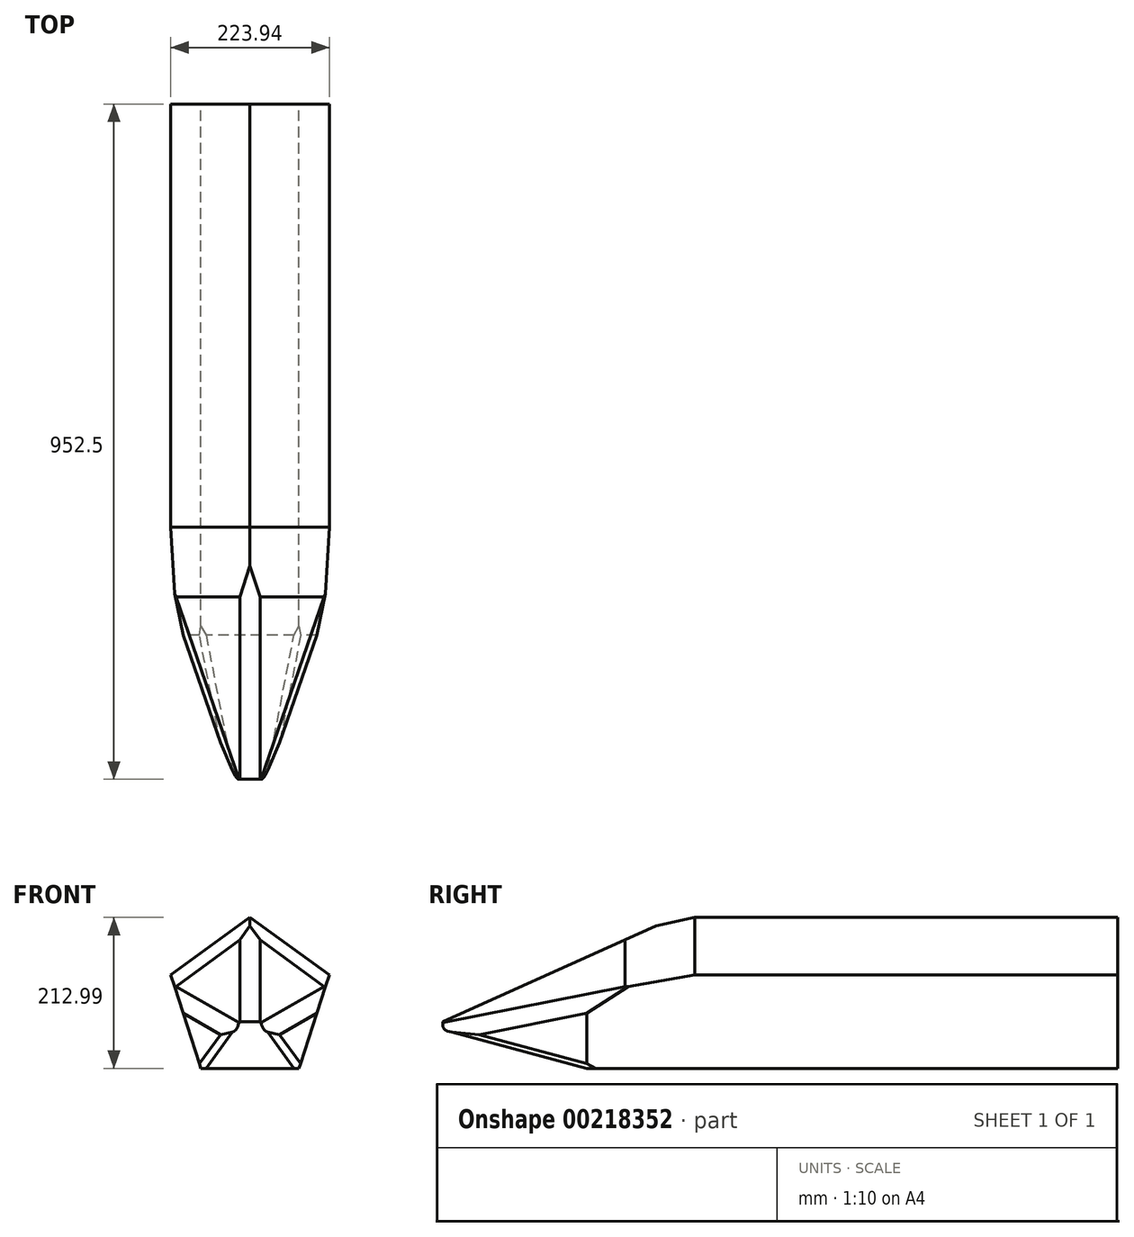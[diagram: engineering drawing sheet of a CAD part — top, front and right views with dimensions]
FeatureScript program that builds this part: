
annotation { "Feature Type Name" : "Feature", "Feature Type Description" : "" }
export const myFeature = defineFeature(function(context is Context, id is Id, definition is map)
    precondition{}
    {
        {
            var Q0;
            Q0=qCreatedBy(makeId("Front.planeOp"),FACE);
            var sketch = newSketch(context, id + "F0", { "sketchPlane" : qUnion([Q0])});
            skLineSegment(sketch, "E0", {"start": v(0, 0) * mm, "end": v(0, 95.25) * mm});
            skLineSegment(sketch, "E1", {"start": v(0, 0) * mm, "end": v(0, -95.25) * mm});
            skCircle(sketch, "E2.cCircle", {"center": v(0, 0) * mm, "radius": 95.25 * mm, "construction": true});
            skLineSegment(sketch, "E2.0", {"start": v(69.2, -95.25) * mm, "end": v(-69.2, -95.25) * mm});
            skLineSegment(sketch, "E2.1", {"start": v(-69.2, -95.25) * mm, "end": v(-111.97, 36.38) * mm});
            skLineSegment(sketch, "E2.2", {"start": v(-111.97, 36.38) * mm, "end": v(0, 117.74) * mm});
            skLineSegment(sketch, "E2.3", {"start": v(0, 117.74) * mm, "end": v(111.97, 36.38) * mm});
            skLineSegment(sketch, "E2.4", {"start": v(111.97, 36.38) * mm, "end": v(69.2, -95.25) * mm});
            skPoint(sketch, "E2.0.midPoint", {"position": v(0, -95.25) * mm});
            skSolve(sketch);
        }
        {
            var Q0;
            {var subQ0=sQuery(id+"F0.wireOp",EDGE,"E2.1");Q0=makeQuery(id+"F0.imprint","IMPRINT",FACE,{"disambiguationData":[TD([[makeQuery(id+"F0.imprint","IMPRINT",EDGE,{"derivedFrom":subQ0}),-1.0]])]});}
            extrude(context, id + "F1", {"entities" : qUnion([Q0]), "depth" : 952.5 * mm});
        }
        {
            var Q0;
            Q0=makeQuery(id+"F1.opExtrude","CAP_EDGE",EDGE,{"disambiguationData":[OSD([sQuery(id+"F0.wireOp",EDGE,"E2.1")])],"isStart":false});
            var Q1;
            Q1=makeQuery(id+"F1.opExtrude","CAP_EDGE",EDGE,{"disambiguationData":[OSD([sQuery(id+"F0.wireOp",EDGE,"E2.0")])],"isStart":false});
            var Q2;
            Q2=makeQuery(id+"F1.opExtrude","CAP_EDGE",EDGE,{"disambiguationData":[OSD([sQuery(id+"F0.wireOp",EDGE,"E2.4")])],"isStart":false});
            chamfer(context, id + "F2", {"entities" : qUnion([Q0, Q1, Q2]), "chamferType" : ChamferType.OFFSET_ANGLE, "width" : 203.2 * mm, "oppositeDirection" : false, "angle" : 15 * degree, "tangentPropagation" : true});
        }
        {
            var Q0;
            Q0=makeQuery(id+"F1.opExtrude","CAP_EDGE",EDGE,{"disambiguationData":[OSD([sQuery(id+"F0.wireOp",EDGE,"E2.3")])],"isStart":false});
            var Q1;
            Q1=makeQuery(id+"F1.opExtrude","CAP_EDGE",EDGE,{"disambiguationData":[OSD([sQuery(id+"F0.wireOp",EDGE,"E2.2")])],"isStart":false});
            chamfer(context, id + "F3", {"entities" : qUnion([Q0, Q1]), "chamferType" : ChamferType.OFFSET_ANGLE, "width" : 304.8 * mm, "oppositeDirection" : false, "angle" : 20 * degree, "tangentPropagation" : true});
        }
        {
            var Q0;
            {var subQ0=sQuery(id+"F0.wireOp",EDGE,"E2.2");Q0=makeQuery(id+"F3.opChamfer","BLEND_EDGE",EDGE,{"blendedFrom":[makeQuery(id+"F1.opExtrude","CAP_EDGE",EDGE,{"disambiguationData":[OSD([subQ0])],"isStart":false}),makeQuery(id+"F1.opExtrude","SWEPT_FACE",FACE,{"disambiguationData":[OSD([subQ0])]})],"blendedInto":[makeQuery(id+"F1.opExtrude","SWEPT_FACE",FACE,{"disambiguationData":[OSD([subQ0])]})]});}
            var Q1;
            {var subQ0=sQuery(id+"F0.wireOp",EDGE,"E2.3");Q1=makeQuery(id+"F3.opChamfer","BLEND_EDGE",EDGE,{"blendedFrom":[makeQuery(id+"F1.opExtrude","CAP_EDGE",EDGE,{"disambiguationData":[OSD([subQ0])],"isStart":false}),makeQuery(id+"F1.opExtrude","SWEPT_FACE",FACE,{"disambiguationData":[OSD([subQ0])]})],"blendedInto":[makeQuery(id+"F1.opExtrude","SWEPT_FACE",FACE,{"disambiguationData":[OSD([subQ0])]})]});}
            chamfer(context, id + "F4", {"entities" : qUnion([Q0, Q1]), "chamferType" : ChamferType.OFFSET_ANGLE, "width" : 50.8 * mm, "oppositeDirection" : true, "angle" : 10 * degree, "tangentPropagation" : true});
        }
        {
            var Q0;
            Q0=makeQuery(id+"F3.opChamfer","BLEND_EDGE",EDGE,{"blendedFrom":[makeQuery(id+"F1.opExtrude","CAP_EDGE",EDGE,{"disambiguationData":[OSD([sQuery(id+"F0.wireOp",EDGE,"E2.2")])],"isStart":false}),makeQuery(id+"F1.opExtrude","CAP_EDGE",EDGE,{"disambiguationData":[OSD([sQuery(id+"F0.wireOp",EDGE,"E2.3")])],"isStart":false})],"blendedInto":[]});
            var Q1;
            Q1=makeQuery(id+"F3.opChamfer","BLEND_EDGE",EDGE,{"blendedFrom":[makeQuery(id+"F1.opExtrude","CAP_EDGE",EDGE,{"disambiguationData":[OSD([sQuery(id+"F0.wireOp",EDGE,"E2.3")])],"isStart":false}),makeQuery(id+"F2.opChamfer","BLEND_FACE",FACE,{"disambiguationData":[OSD([sQuery(id+"F0.wireOp",EDGE,"E2.4")])]})],"blendedInto":[makeQuery(id+"F2.opChamfer","BLEND_FACE",FACE,{"disambiguationData":[OSD([sQuery(id+"F0.wireOp",EDGE,"E2.4")])]})]});
            var Q2;
            Q2=makeQuery(id+"F3.opChamfer","BLEND_EDGE",EDGE,{"blendedFrom":[makeQuery(id+"F1.opExtrude","CAP_EDGE",EDGE,{"disambiguationData":[OSD([sQuery(id+"F0.wireOp",EDGE,"E2.2")])],"isStart":false}),makeQuery(id+"F2.opChamfer","BLEND_FACE",FACE,{"disambiguationData":[OSD([sQuery(id+"F0.wireOp",EDGE,"E2.1")])]})],"blendedInto":[makeQuery(id+"F2.opChamfer","BLEND_FACE",FACE,{"disambiguationData":[OSD([sQuery(id+"F0.wireOp",EDGE,"E2.1")])]})]});
            chamfer(context, id + "F5", {"entities" : qUnion([Q0, Q1, Q2]), "width" : 25.4 * mm, "tangentPropagation" : true});
        }
        {
            var Q0;
            Q0=makeQuery(id+"F2.opChamfer","BLEND_EDGE",EDGE,{"blendedFrom":[makeQuery(id+"F1.opExtrude","CAP_EDGE",EDGE,{"disambiguationData":[OSD([sQuery(id+"F0.wireOp",EDGE,"E2.0")])],"isStart":false}),makeQuery(id+"F1.opExtrude","CAP_EDGE",EDGE,{"disambiguationData":[OSD([sQuery(id+"F0.wireOp",EDGE,"E2.1")])],"isStart":false})],"blendedInto":[]});
            var Q1;
            Q1=makeQuery(id+"F2.opChamfer","BLEND_EDGE",EDGE,{"blendedFrom":[makeQuery(id+"F1.opExtrude","CAP_EDGE",EDGE,{"disambiguationData":[OSD([sQuery(id+"F0.wireOp",EDGE,"E2.0")])],"isStart":false}),makeQuery(id+"F1.opExtrude","CAP_EDGE",EDGE,{"disambiguationData":[OSD([sQuery(id+"F0.wireOp",EDGE,"E2.4")])],"isStart":false})],"blendedInto":[]});
            chamfer(context, id + "F6", {"entities" : qUnion([Q0, Q1]), "width" : 10.16 * mm, "tangentPropagation" : true});
        }
        {
            var Q0;
            {var subQ0=sQuery(id+"F0.wireOp",EDGE,"E2.0");Q0=makeQuery(id+"F2.opChamfer","BLEND_EDGE",EDGE,{"blendedFrom":[makeQuery(id+"F1.opExtrude","CAP_EDGE",EDGE,{"disambiguationData":[OSD([subQ0])],"isStart":false}),makeQuery(id+"F1.opExtrude","CAP_FACE",FACE,{"disambiguationData":[OSD([subQ0,sQuery(id+"F0.wireOp",EDGE,"E2.1"),sQuery(id+"F0.wireOp",EDGE,"E2.2"),sQuery(id+"F0.wireOp",EDGE,"E2.3"),sQuery(id+"F0.wireOp",EDGE,"E2.4")])],"isStart":false})],"blendedInto":[makeQuery(id+"F1.opExtrude","CAP_FACE",FACE,{"disambiguationData":[OSD([subQ0,sQuery(id+"F0.wireOp",EDGE,"E2.1"),sQuery(id+"F0.wireOp",EDGE,"E2.2"),sQuery(id+"F0.wireOp",EDGE,"E2.3"),sQuery(id+"F0.wireOp",EDGE,"E2.4")])],"isStart":false})]});}
            fillet(context, id + "F7", {"entities" : qUnion([Q0]), "radius" : 8.9 * mm, "tangentPropagation" : true, "allowEdgeOverflow" : false});
        }
    });
